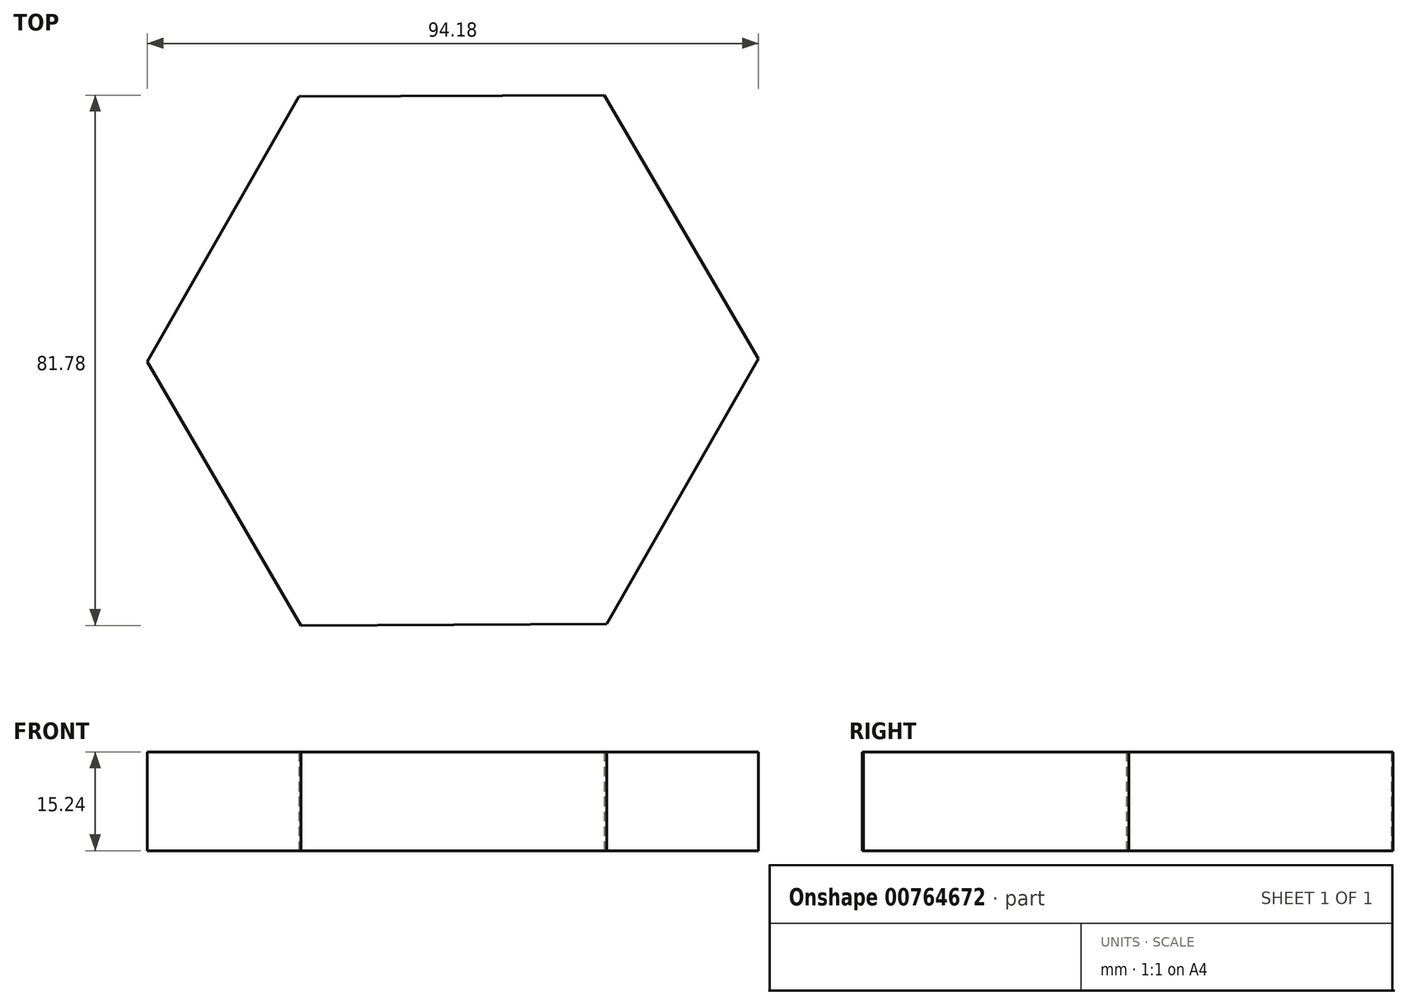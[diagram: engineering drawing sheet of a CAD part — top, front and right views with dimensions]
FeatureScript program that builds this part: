
annotation { "Feature Type Name" : "Feature", "Feature Type Description" : "" }
export const myFeature = defineFeature(function(context is Context, id is Id, definition is map)
    precondition{}
    {
        {
            var Q0;
            Q0=qCreatedBy(makeId("Top.planeOp"),FACE);
            var sketch = newSketch(context, id + "F0", { "sketchPlane" : qUnion([Q0])});
            skCircle(sketch, "E0.cCircle", {"center": v(0, 0) * mm, "radius": 40.78 * mm, "construction": true});
            skLineSegment(sketch, "E0.0", {"start": v(-47.1, -0.2) * mm, "end": v(-23.73, 40.68) * mm});
            skLineSegment(sketch, "E0.1", {"start": v(-23.73, 40.68) * mm, "end": v(23.37, 40.89) * mm});
            skLineSegment(sketch, "E0.2", {"start": v(23.37, 40.89) * mm, "end": v(47.1, 0.2) * mm});
            skLineSegment(sketch, "E0.3", {"start": v(47.1, 0.2) * mm, "end": v(23.73, -40.68) * mm});
            skLineSegment(sketch, "E0.4", {"start": v(23.73, -40.68) * mm, "end": v(-23.37, -40.89) * mm});
            skLineSegment(sketch, "E0.5", {"start": v(-23.37, -40.89) * mm, "end": v(-47.1, -0.2) * mm});
            skPoint(sketch, "E0.0.midPoint", {"position": v(-35.41, 20.23) * mm});
            skSolve(sketch);
        }
        {
            var Q0;
            Q0=makeQuery(id+"F0.imprint","IMPRINT",FACE,{"disambiguationData":[TD([[makeQuery(id+"F0.imprint","IMPRINT",EDGE,{"derivedFrom":sQuery(id+"F0.wireOp",EDGE,"E0.0")}),-1.0]])]});
            extrude(context, id + "F1", {"entities" : qUnion([Q0]), "depth" : 15.24 * mm, "offsetDistance" : 25.4 * mm});
        }
    });
